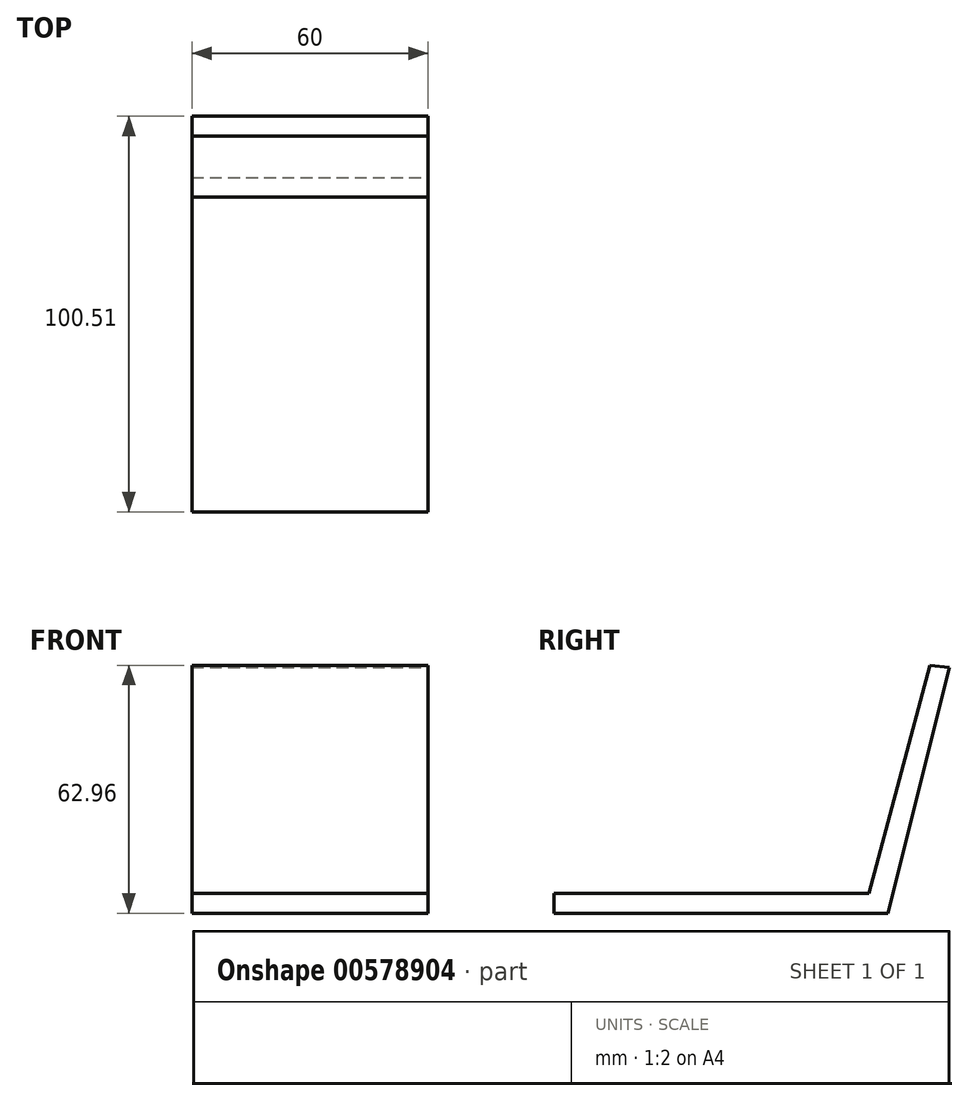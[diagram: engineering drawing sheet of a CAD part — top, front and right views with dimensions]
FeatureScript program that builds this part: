
annotation { "Feature Type Name" : "Feature", "Feature Type Description" : "" }
export const myFeature = defineFeature(function(context is Context, id is Id, definition is map)
    precondition{}
    {
        {
            var Q0;
            Q0=qCreatedBy(makeId("Right.planeOp"),FACE);
            var sketch = newSketch(context, id + "F0", { "sketchPlane" : qUnion([Q0])});
            skLineSegment(sketch, "E0", {"start": v(-95.53, 0) * mm, "end": v(-15.53, 0) * mm});
            skLineSegment(sketch, "E1", {"start": v(-15.53, 0) * mm, "end": v(0, 57.96) * mm});
            skLineSegment(sketch, "E2", {"start": v(-95.53, 0) * mm, "end": v(-95.53, -5) * mm});
            skLineSegment(sketch, "E3", {"start": v(-95.53, -5) * mm, "end": v(-10.63, -5) * mm});
            skLineSegment(sketch, "E4", {"start": v(-10.63, -5) * mm, "end": v(4.98, 57.48) * mm});
            skLineSegment(sketch, "E5", {"start": v(4.98, 57.48) * mm, "end": v(0, 57.96) * mm});
            skSolve(sketch);
        }
        {
            var Q0;
            Q0 = qSketchRegion(id + "F0", true);
            extrude(context, id + "F1", {"entities" : qUnion([Q0]), "oppositeDirection" : true, "depth" : 60 * mm, "offsetDistance" : 25 * mm});
        }
    });
